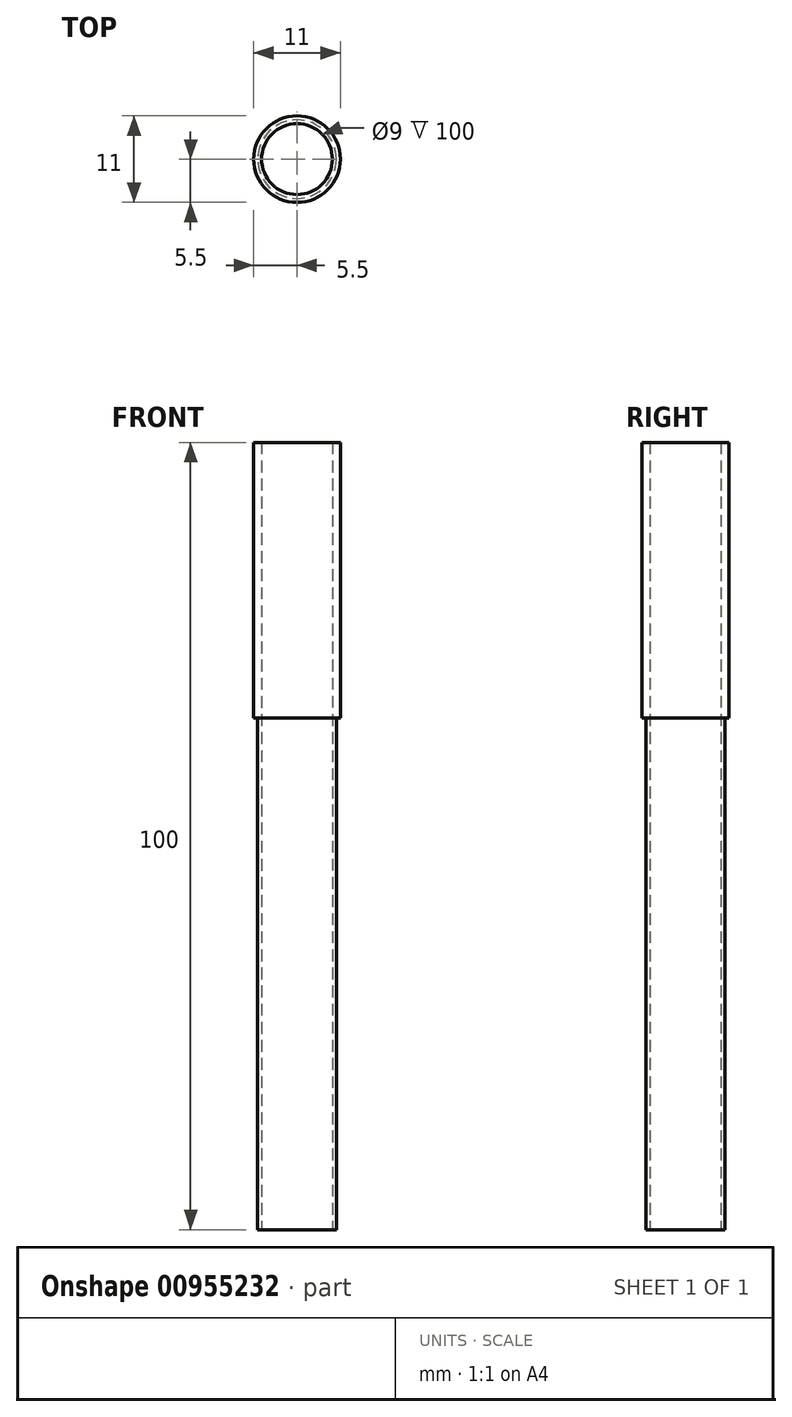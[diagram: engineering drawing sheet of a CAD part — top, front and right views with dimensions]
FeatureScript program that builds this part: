
annotation { "Feature Type Name" : "Feature", "Feature Type Description" : "" }
export const myFeature = defineFeature(function(context is Context, id is Id, definition is map)
    precondition{}
    {
        {
            var Q0;
            Q0=qCreatedBy(makeId("Top.planeOp"),FACE);
            var sketch = newSketch(context, id + "F0", { "sketchPlane" : qUnion([Q0])});
            skCircle(sketch, "E0", {"center": v(0, 0) * mm, "radius": 5 * mm});
            skSolve(sketch);
        }
        {
            var Q0;
            Q0=makeQuery(id+"F0.imprint","IMPRINT",FACE,{"disambiguationData":[TD([[makeQuery(id+"F0.imprint","IMPRINT",EDGE,{"derivedFrom":sQuery(id+"F0.wireOp",EDGE,"E0")}),1.0]])]});
            extrude(context, id + "F1", {"entities" : qUnion([Q0]), "depth" : 50 * mm, "offsetDistance" : 25.4 * mm});
        }
        {
            var Q0;
            Q0=makeQuery(id+"F1.opExtrude","SWEPT_BODY",BODY,{"disambiguationData":[OSD([sQuery(id+"F0.wireOp",EDGE,"E0")])]});
            var Q1;
            Q1=makeQuery(id+"F1.opExtrude","CAP_FACE",FACE,{"disambiguationData":[OSD([sQuery(id+"F0.wireOp",EDGE,"E0")])],"isStart":true});
            mirror(context, id + "F2", {"operationType" : NewBodyOperationType.ADD, "entities" : qUnion([Q0]), "mirrorPlane" : qUnion([Q1])});
        }
        {
            var Q0;
            Q0=makeQuery(id+"F2.opPattern","COPY",FACE,{"derivedFrom":makeQuery(id+"F1.opExtrude","CAP_FACE",FACE,{"disambiguationData":[OSD([sQuery(id+"F0.wireOp",EDGE,"E0")])],"isStart":false}),"instanceName":"1"});
            var sketch = newSketch(context, id + "F3", { "sketchPlane" : qUnion([Q0])});
            skCircle(sketch, "E1", {"center": v(0, 0) * mm, "radius": 4.5 * mm});
            skSolve(sketch);
        }
        {
            var Q0;
            Q0=makeQuery(id+"F3.imprint","IMPRINT",FACE,{"disambiguationData":[TD([[makeQuery(id+"F3.imprint","IMPRINT",EDGE,{"derivedFrom":sQuery(id+"F3.wireOp",EDGE,"E1")}),1.0]])]});
            extrude(context, id + "F4", {"entities" : qUnion([Q0]), "operationType" : NewBodyOperationType.REMOVE, "oppositeDirection" : true, "depth" : 100 * mm, "offsetDistance" : 25 * mm});
        }
        {
            var Q0;
            Q0=makeQuery(id+"F1.opExtrude","CAP_FACE",FACE,{"disambiguationData":[OSD([sQuery(id+"F0.wireOp",EDGE,"E0")])],"isStart":false});
            var sketch = newSketch(context, id + "F5", { "sketchPlane" : qUnion([Q0])});
            skCircle(sketch, "E2", {"center": v(0, 0) * mm, "radius": 5.5 * mm});
            skSolve(sketch);
        }
        {
            var Q0;
            Q0=makeQuery(id+"F5.imprint","IMPRINT",FACE,{"disambiguationData":[TD([[makeQuery(id+"F5.imprint","IMPRINT",EDGE,{"derivedFrom":sQuery(id+"F5.wireOp",EDGE,"E2")}),1.0]])]});
            extrude(context, id + "F6", {"entities" : qUnion([Q0]), "operationType" : NewBodyOperationType.ADD, "oppositeDirection" : true, "depth" : 35 * mm, "offsetDistance" : 25 * mm});
        }
    });
